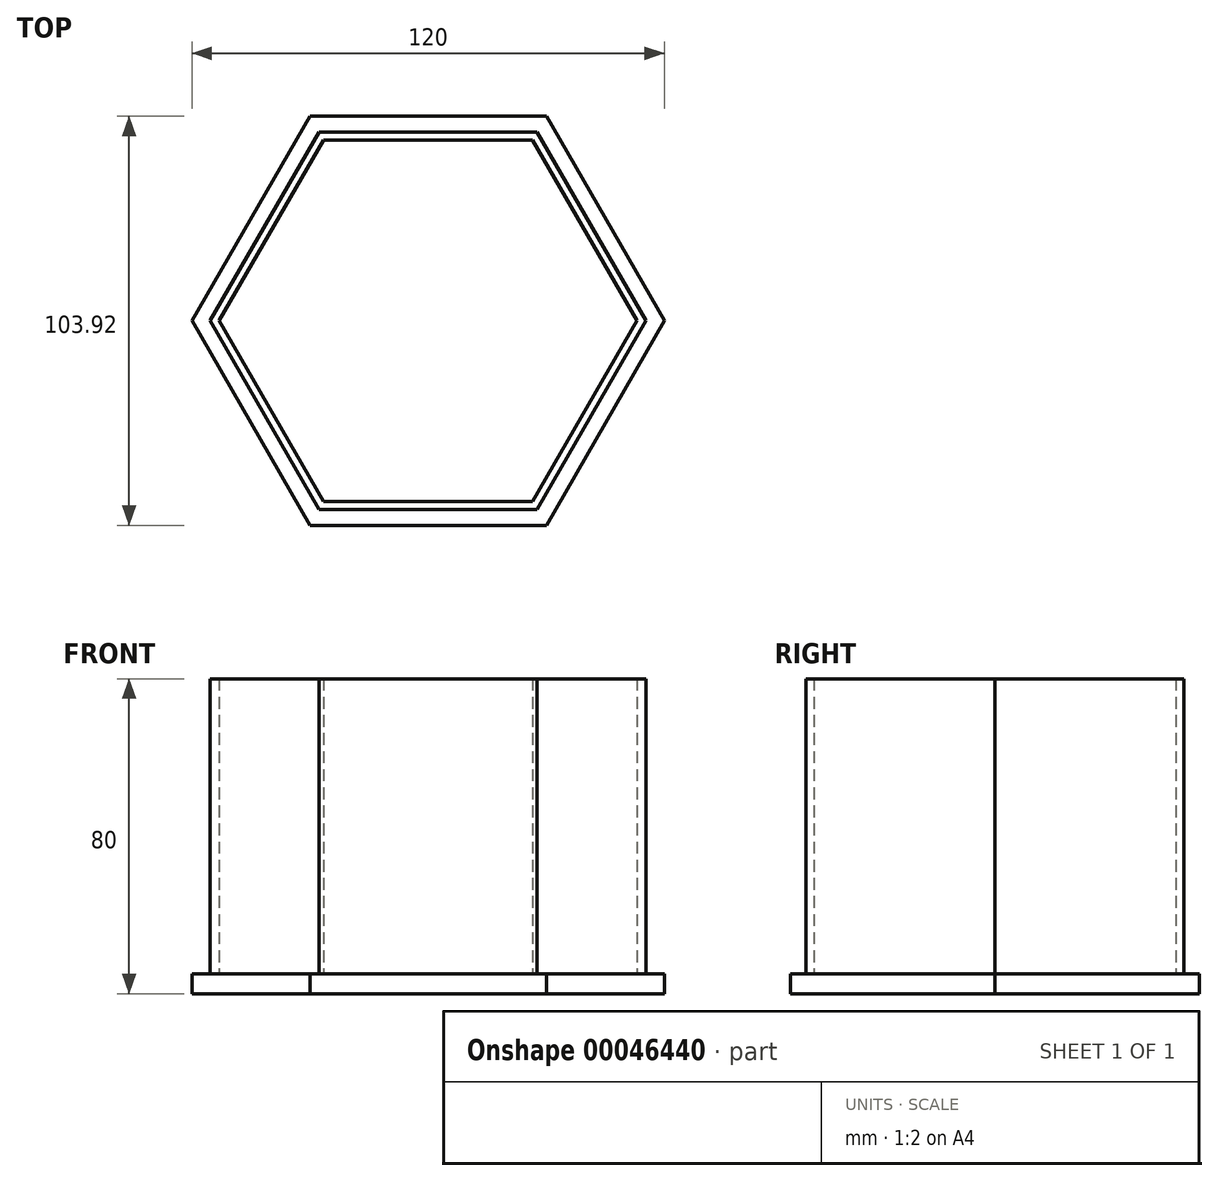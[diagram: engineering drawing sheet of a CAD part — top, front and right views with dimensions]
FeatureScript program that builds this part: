
annotation { "Feature Type Name" : "Feature", "Feature Type Description" : "" }
export const myFeature = defineFeature(function(context is Context, id is Id, definition is map)
    precondition{}
    {
        {
            var Q0;
            Q0=qCreatedBy(makeId("Top.planeOp"),FACE);
            var sketch = newSketch(context, id + "F0", { "sketchPlane" : qUnion([Q0])});
            skCircle(sketch, "E0.cCircle", {"center": v(0, 0) * mm, "radius": 60 * mm, "construction": true});
            skLineSegment(sketch, "E0.0", {"start": v(60, 0) * mm, "end": v(30, -51.96) * mm});
            skLineSegment(sketch, "E0.1", {"start": v(30, -51.96) * mm, "end": v(-30, -51.96) * mm});
            skLineSegment(sketch, "E0.2", {"start": v(-30, -51.96) * mm, "end": v(-60, 0) * mm});
            skLineSegment(sketch, "E0.3", {"start": v(-60, 0) * mm, "end": v(-30, 51.96) * mm});
            skLineSegment(sketch, "E0.4", {"start": v(-30, 51.96) * mm, "end": v(30, 51.96) * mm});
            skLineSegment(sketch, "E0.5", {"start": v(30, 51.96) * mm, "end": v(60, 0) * mm});
            skSolve(sketch);
        }
        {
            var Q0;
            Q0=makeQuery(id+"F0.imprint","IMPRINT",FACE,{"disambiguationData":[TD([[makeQuery(id+"F0.imprint","IMPRINT",EDGE,{"derivedFrom":sQuery(id+"F0.wireOp",EDGE,"E0.0")}),-1.0]])]});
            extrude(context, id + "F1", {"entities" : qUnion([Q0]), "depth" : 5 * mm});
        }
        {
            var Q0;
            Q0=makeQuery(id+"F1.opExtrude","CAP_FACE",FACE,{"disambiguationData":[OSD([sQuery(id+"F0.wireOp",EDGE,"E0.0"),sQuery(id+"F0.wireOp",EDGE,"E0.1"),sQuery(id+"F0.wireOp",EDGE,"E0.2"),sQuery(id+"F0.wireOp",EDGE,"E0.3"),sQuery(id+"F0.wireOp",EDGE,"E0.4"),sQuery(id+"F0.wireOp",EDGE,"E0.5")])],"isStart":false});
            var sketch = newSketch(context, id + "F2", { "sketchPlane" : qUnion([Q0])});
            skLineSegment(sketch, "E1.0", {"start": v(-55.38, 0) * mm, "end": v(-27.7, 47.96) * mm});
            skLineSegment(sketch, "E1.1", {"start": v(27.7, 47.96) * mm, "end": v(55.38, 0) * mm});
            skLineSegment(sketch, "E1.2", {"start": v(55.38, 0) * mm, "end": v(27.7, -47.96) * mm});
            skLineSegment(sketch, "E1.3", {"start": v(-27.7, 47.96) * mm, "end": v(27.7, 47.96) * mm});
            skLineSegment(sketch, "E1.4", {"start": v(27.7, -47.96) * mm, "end": v(-27.7, -47.96) * mm});
            skLineSegment(sketch, "E1.5", {"start": v(-27.7, -47.96) * mm, "end": v(-55.38, 0) * mm});
            skLineSegment(sketch, "E2.0", {"start": v(-53.07, 0) * mm, "end": v(-26.54, 45.96) * mm});
            skLineSegment(sketch, "E2.1", {"start": v(26.54, 45.96) * mm, "end": v(53.07, 0) * mm});
            skLineSegment(sketch, "E2.2", {"start": v(53.07, 0) * mm, "end": v(26.54, -45.96) * mm});
            skLineSegment(sketch, "E2.3", {"start": v(-26.54, 45.96) * mm, "end": v(26.54, 45.96) * mm});
            skLineSegment(sketch, "E2.4", {"start": v(26.54, -45.96) * mm, "end": v(-26.54, -45.96) * mm});
            skLineSegment(sketch, "E2.5", {"start": v(-26.54, -45.96) * mm, "end": v(-53.07, 0) * mm});
            skSolve(sketch);
        }
        {
            var Q0;
            Q0=makeQuery(id+"F2.imprint","IMPRINT",FACE,{"disambiguationData":[TD([[makeQuery(id+"F2.imprint","IMPRINT",EDGE,{"derivedFrom":sQuery(id+"F2.wireOp",EDGE,"E1.0")}),-1.0]])]});
            extrude(context, id + "F3", {"entities" : qUnion([Q0]), "operationType" : NewBodyOperationType.ADD, "depth" : 75 * mm});
        }
    });
